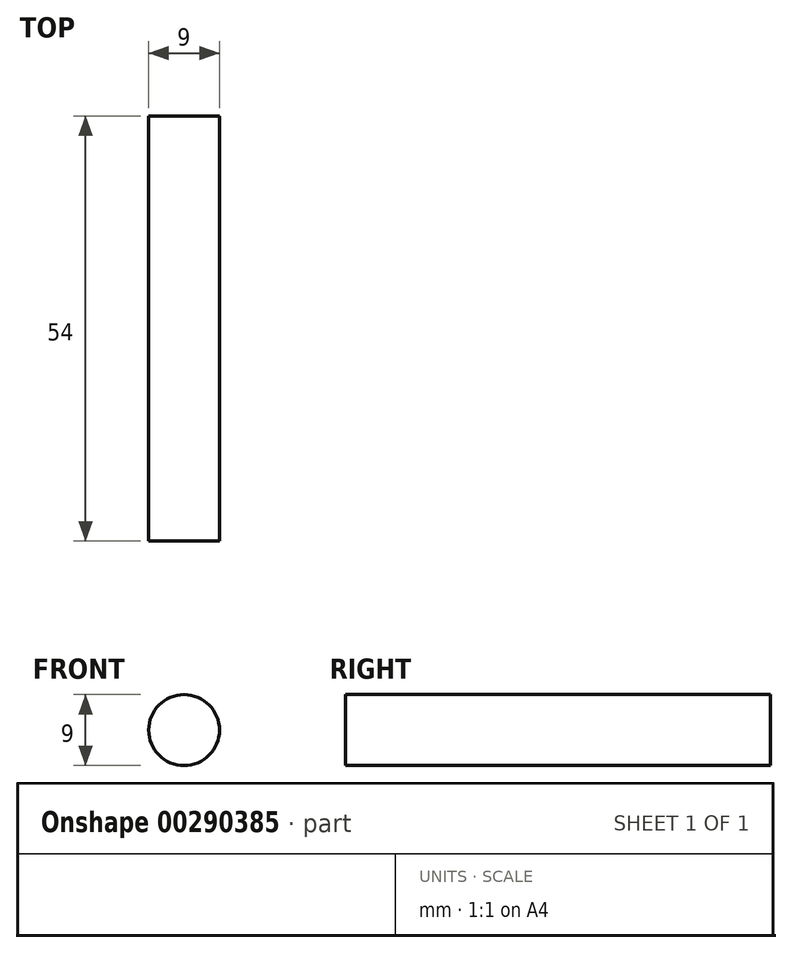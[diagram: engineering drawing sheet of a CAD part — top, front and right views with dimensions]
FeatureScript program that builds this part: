
annotation { "Feature Type Name" : "Feature", "Feature Type Description" : "" }
export const myFeature = defineFeature(function(context is Context, id is Id, definition is map)
    precondition{}
    {
        {
            var Q0;
            Q0=qCreatedBy(makeId("Front.planeOp"),FACE);
            var sketch = newSketch(context, id + "F0", { "sketchPlane" : qUnion([Q0])});
            skCircle(sketch, "E0", {"center": v(-20.66, 23.19) * mm, "radius": 4.5 * mm});
            skSolve(sketch);
        }
        {
            var Q0;
            Q0 = qSketchRegion(id + "F0", true);
            extrude(context, id + "F1", {"entities" : qUnion([Q0]), "depth" : 54 * mm});
        }
    });
